# Revit family: Towel_Ring-Wall_Mounted-American_Standard-Edgemere-7018190_Series
name_source: partatom
category: Specialty Equipment
units: mm (PartAtom-declared; Revit-internal decimal feet)

## family parameters
Cut with Voids When Loaded = No
Host = Face
OmniClass Number = 23.40.20.21.27
OmniClass Title = Towel Bars
Part Type = Normal
Room Calculation Point = No
Round Connector Dimension = Use Diameter
Shared = Yes

## types (4) — shared parameters
Assembly Code = C1030220
Default Elevation = 40"
Description = Edgemere Towel Ring
Height = 8"
Installation Instruction Link = https://lixil.cdn.celum.cloud
Installation Type = Wall Mounted
Length = 7 1/4"
Manufacturer = American Standard
Price = Prices may vary. Please consult Manufacturer Representative for most up-to-date price list.
Product Documentation Link = https://lixil.cdn.celum.cloud
Product Page URL = https://www.americanstandard-us.com
Revised Date = 02/21/2024
URL = http://www.americanstandard-us.com
Warranty Information = Lifetime Warranty
Width = 2 7/8"

## per-type parameters (varying)
| type | Finish | Material |
| 7018190.002 | Metal-American Standard-002-Polished Chrome | Metal-American Standard-002-Polished Chrome |
| 7018190.243 | Metal-American Standard-243-Matte Black | Metal-American Standard-243-Matte Black |
| 7018190.295 | Metal-American Standard-295-Brushed Nickel | Metal-American Standard-295-Brushed Nickel |
| 7018190.278 | Metal-American Standard-278-Legacy Bronze | Metal-American Standard-278-Legacy Bronze |

note: column(s) folded — value = type name in every type: Model

## geometry (parser evidence)
native form markers: Sweep x2
no freeform markers — native parametric forms only
